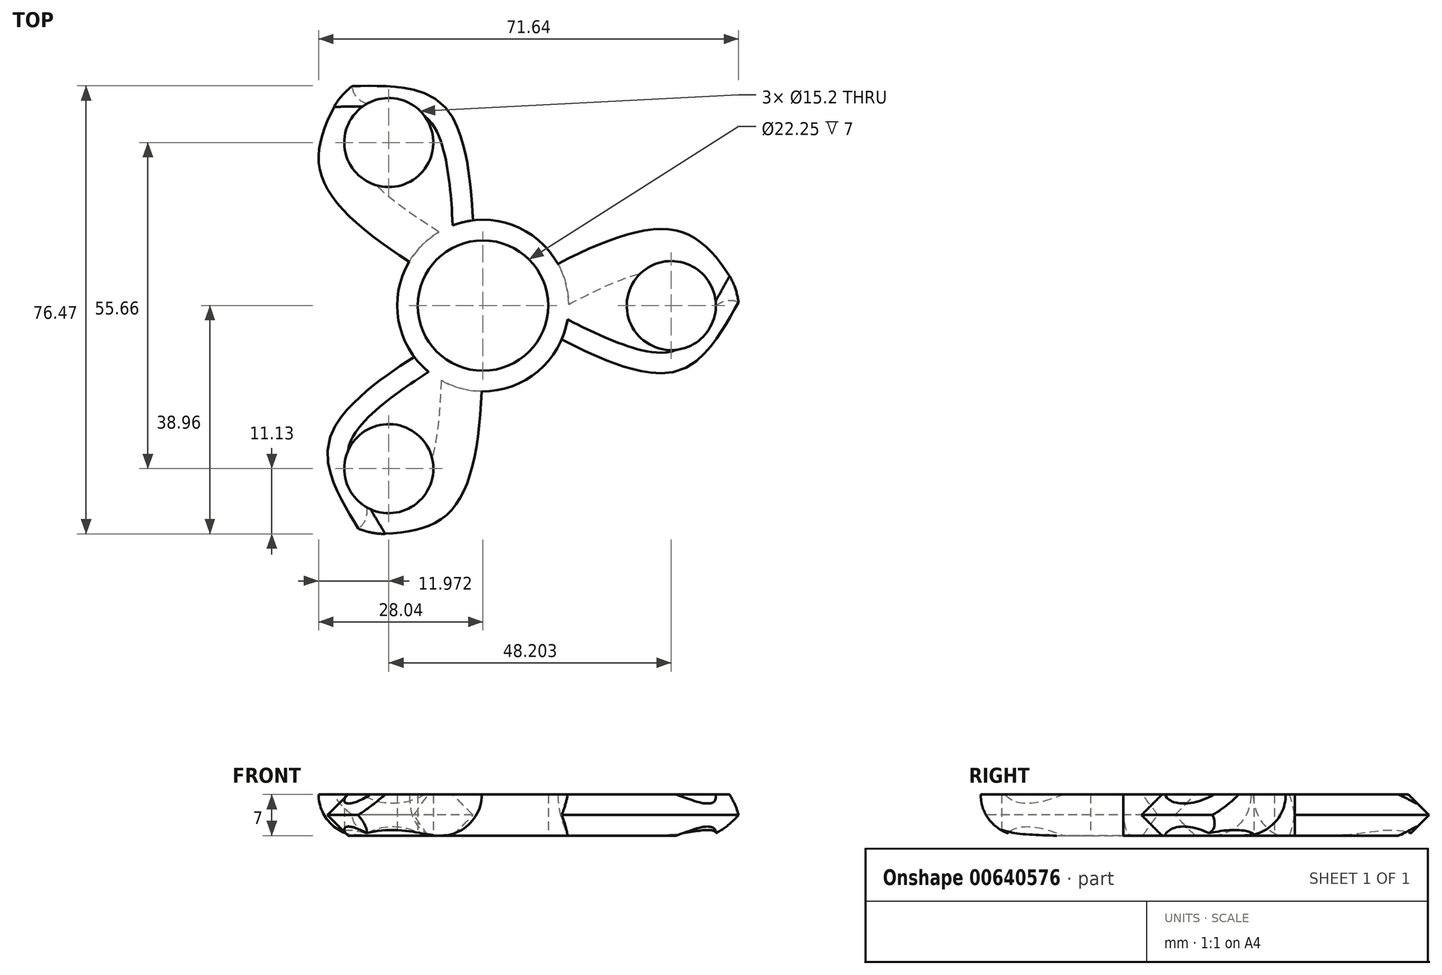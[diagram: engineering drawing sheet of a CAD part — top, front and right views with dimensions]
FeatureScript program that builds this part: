
annotation { "Feature Type Name" : "Feature", "Feature Type Description" : "" }
export const myFeature = defineFeature(function(context is Context, id is Id, definition is map)
    precondition{}
    {
        {
            var Q0;
            Q0=qCreatedBy(makeId("Top.planeOp"),FACE);
            var sketch = newSketch(context, id + "F0", { "sketchPlane" : qUnion([Q0])});
            skCircle(sketch, "E0", {"center": v(0, 0) * mm, "radius": 11.13 * mm});
            skLineSegment(sketch, "E1", {"start": v(-22.5, 38.97) * mm, "end": v(0, 0) * mm});
            skFitSpline(sketch, "E2.MirrorCS", {"points": [v(-22.5, 38.97) * mm, v(-5.47, 35.03) * mm, v(0, 0) * mm], "startDerivative": vector(47.89, 0.77) * mm, "endDerivative": vector(-0.1, -74.33) * mm});
            skFitSpline(sketch, "E3.MirrorCS", {"points": [v(-22.5, 38.97) * mm, v(-27.6, 22.25) * mm, v(0, 0) * mm], "startDerivative": vector(-24.6, -41.09) * mm, "endDerivative": vector(64.42, -37.09) * mm});
            skLineSegment(sketch, "E4.MirrorCS", {"start": v(-22.5, -38.97) * mm, "end": v(0, 0) * mm});
            skLineSegment(sketch, "E5", {"start": v(0, 0) * mm, "end": v(45, 0) * mm});
            skFitSpline(sketch, "E6.MirrorCS", {"points": [v(-22.5, -38.97) * mm, v(-27.6, -22.25) * mm, v(0, 0) * mm], "startDerivative": vector(-24.6, 41.09) * mm, "endDerivative": vector(64.42, 37.09) * mm});
            skCircle(sketch, "E7", {"center": v(-16.07, 27.83) * mm, "radius": 7.6 * mm});
            skCircle(sketch, "E8.MirrorC", {"center": v(-16.07, -27.83) * mm, "radius": 7.6 * mm});
            skLineSegment(sketch, "E9.MirrorCS", {"start": v(0, 0) * mm, "end": v(-22.5, 38.97) * mm});
            skCircle(sketch, "E10", {"center": v(32.14, 0) * mm, "radius": 7.6 * mm});
            skCircle(sketch, "E11", {"center": v(0, 0) * mm, "radius": 14.64 * mm});
            skFitSpline(sketch, "E12.MirrorCS", {"points": [v(45, 0) * mm, v(33.07, 12.78) * mm, v(0, 0) * mm], "startDerivative": vector(-23.28, 41.85) * mm, "endDerivative": vector(-64.33, -37.24) * mm});
            skFitSpline(sketch, "E13.MirrorCS", {"points": [v(-22.5, -38.97) * mm, v(-5.47, -35.03) * mm, v(0, 0) * mm], "startDerivative": vector(47.89, -0.77) * mm, "endDerivative": vector(-0.1, 74.33) * mm});
            skFitSpline(sketch, "E14.MirrorCS", {"points": [v(45, 0) * mm, v(33.07, -12.78) * mm, v(0, 0) * mm], "startDerivative": vector(-23.28, -41.85) * mm, "endDerivative": vector(-64.33, 37.24) * mm});
            skLineSegment(sketch, "E15", {"start": v(-12.27, -21.25) * mm, "end": v(0, 0) * mm});
            skLineSegment(sketch, "E16", {"start": v(0, 0) * mm, "end": v(24.54, 0) * mm});
            skLineSegment(sketch, "E17", {"start": v(24.54, 0) * mm, "end": v(0, 0) * mm});
            skLineSegment(sketch, "E18", {"start": v(0, 0) * mm, "end": v(-12.27, 21.25) * mm});
            skSolve(sketch);
        }
        {
            var Q0;
            Q0 = qSketchRegion(id + "F0", true);
            extrude(context, id + "F1", {"entities" : qUnion([Q0]), "depth" : 7 * mm, "offsetDistance" : 25 * mm});
        }
        {
            var Q0;
            Q0=makeQuery(id+"F1.opExtrude","CAP_EDGE",EDGE,{"disambiguationData":[OSD([sQuery(id+"F0.wireOp",EDGE,"E6.MirrorCS")])],"isStart":false});
            var Q1;
            Q1=makeQuery(id+"F1.opExtrude","CAP_EDGE",EDGE,{"disambiguationData":[OSD([sQuery(id+"F0.wireOp",EDGE,"E2.MirrorCS")])],"isStart":false});
            var Q2;
            Q2=makeQuery(id+"F1.opExtrude","CAP_EDGE",EDGE,{"disambiguationData":[OSD([sQuery(id+"F0.wireOp",EDGE,"E14.MirrorCS")])],"isStart":false});
            chamfer(context, id + "F2", {"entities" : qUnion([Q0, Q1, Q2]), "width" : 5 * mm, "tangentPropagation" : true});
        }
        {
            var Q0;
            Q0=makeQuery(id+"F1.opExtrude","CAP_EDGE",EDGE,{"disambiguationData":[OSD([sQuery(id+"F0.wireOp",EDGE,"E6.MirrorCS")])],"isStart":true});
            var Q1;
            Q1=makeQuery(id+"F1.opExtrude","CAP_EDGE",EDGE,{"disambiguationData":[OSD([sQuery(id+"F0.wireOp",EDGE,"E2.MirrorCS")])],"isStart":true});
            var Q2;
            Q2=makeQuery(id+"F1.opExtrude","CAP_EDGE",EDGE,{"disambiguationData":[OSD([sQuery(id+"F0.wireOp",EDGE,"E14.MirrorCS")])],"isStart":true});
            chamfer(context, id + "F3", {"entities" : qUnion([Q0, Q1, Q2]), "width" : 5 * mm, "tangentPropagation" : true});
        }
        {
            var Q0;
            Q0=makeQuery(id+"F1.opExtrude","CAP_EDGE",EDGE,{"disambiguationData":[OSD([sQuery(id+"F0.wireOp",EDGE,"E3.MirrorCS")])],"isStart":true});
            var Q1;
            Q1=makeQuery(id+"F1.opExtrude","CAP_EDGE",EDGE,{"disambiguationData":[OSD([sQuery(id+"F0.wireOp",EDGE,"E13.MirrorCS")])],"isStart":true});
            var Q2;
            Q2=makeQuery(id+"F1.opExtrude","CAP_EDGE",EDGE,{"disambiguationData":[OSD([sQuery(id+"F0.wireOp",EDGE,"E12.MirrorCS")])],"isStart":true});
            fillet(context, id + "F4", {"entities" : qUnion([Q0, Q1, Q2]), "radius" : 7 * mm, "tangentPropagation" : true, "allowEdgeOverflow" : false});
        }
    });
